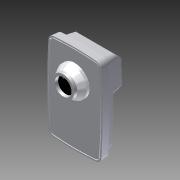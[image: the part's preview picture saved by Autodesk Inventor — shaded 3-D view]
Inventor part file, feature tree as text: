
AUTODESK INVENTOR PART (.ipt)
format: ipt  version: 2014 (Build 180170000, 170)  size: 709,632 bytes
history: native  units: in
note: dims shown in document units (in); Inventor stores cm internally (conversion verified against a paired STEP export)
features: sketch x11, extrude x8, fillet x5, plane x2, revolve x2, other x1, projected_geometry x1
ambient origin geometry x8: Origin, YZ Plane, XZ Plane, XY Plane, X Axis, Y Axis, Z Axis, Center Point
bodies: Solid1 (feature_tree)
feature tree (30):
  extrude  "Extrusion1"  Depth=0.06in
  extrude  "Extrusion2"  Depth=0.05in
  extrude  "Extrusion3"  Depth=0.44in
  extrude  "Extrusion4"  TaperAngle=45.0deg  [1 undecoded]
  plane  "Work Plane1"
  extrude  "Extrusion5"  Depth=2.56in
  extrude  "Extrusion6"  Depth=0.12in TaperAngle=0.0deg
  extrude  "Extrusion7"  TaperAngle=180.0deg  [1 undecoded]
  plane  "Work Plane2"
  revolve  "Revolution3"  [1 undecoded]
  sketch  "Sketch9"  dims[d24=0.0in d25=0.01in d26=0.05in d27=0.05in d28=2.33in d29=3.75in d30=0.12in d31=-0.0687in]
  revolve  "Revolution2"  [1 undecoded]
  fillet  "Fillet1"  Radius=0.05in
  fillet  "Fillet2"  Radius=0.05in
  fillet  "Fillet3"  Radius=2.33in
  fillet  "Fillet4"  Radius=3.75in
  fillet  "Fillet5"  Radius=0.12in
  extrude  "Extrusion8"  [1 undecoded]
  sketch  "Sketch1"  dims[d0=0.335in d1=-0.0344in d2=0.06in]
  sketch  "Sketch2"  dims[d3=0.027in d4=0.05in d5=-0.0344in]
  sketch  "Sketch3"  dims[d6=0.335in d7=-0.0687in d8=0.44in d9=-0.0687in]
  sketch  "Sketch4"  dims[d10=0.25in d11=45.0deg]
  sketch  "Sketch5"  dims[d12=0.0in d13=0.0in d14=2.56in]
  sketch  "Sketch6"  dims[d15=1.25in d16=0.12in d17=0.0in]
  sketch  "Sketch7"  dims[d18=0.25in d19=-0.2061in d20=180.0deg]
  other  "Work Axis1"
  sketch  "Sketch8"  dims[d22=90.0deg d23=0.02in]
  sketch  "Sketch10"  dims[d32=90.0deg]
  sketch  "Sketch11"
  projected_geometry  "Project Cut Edges1"
note: 5 required parameter values undecoded (feature->parameter linkage not recoverable at this tier; creation-order binding heuristic only, values carry confidence <= 0.55)